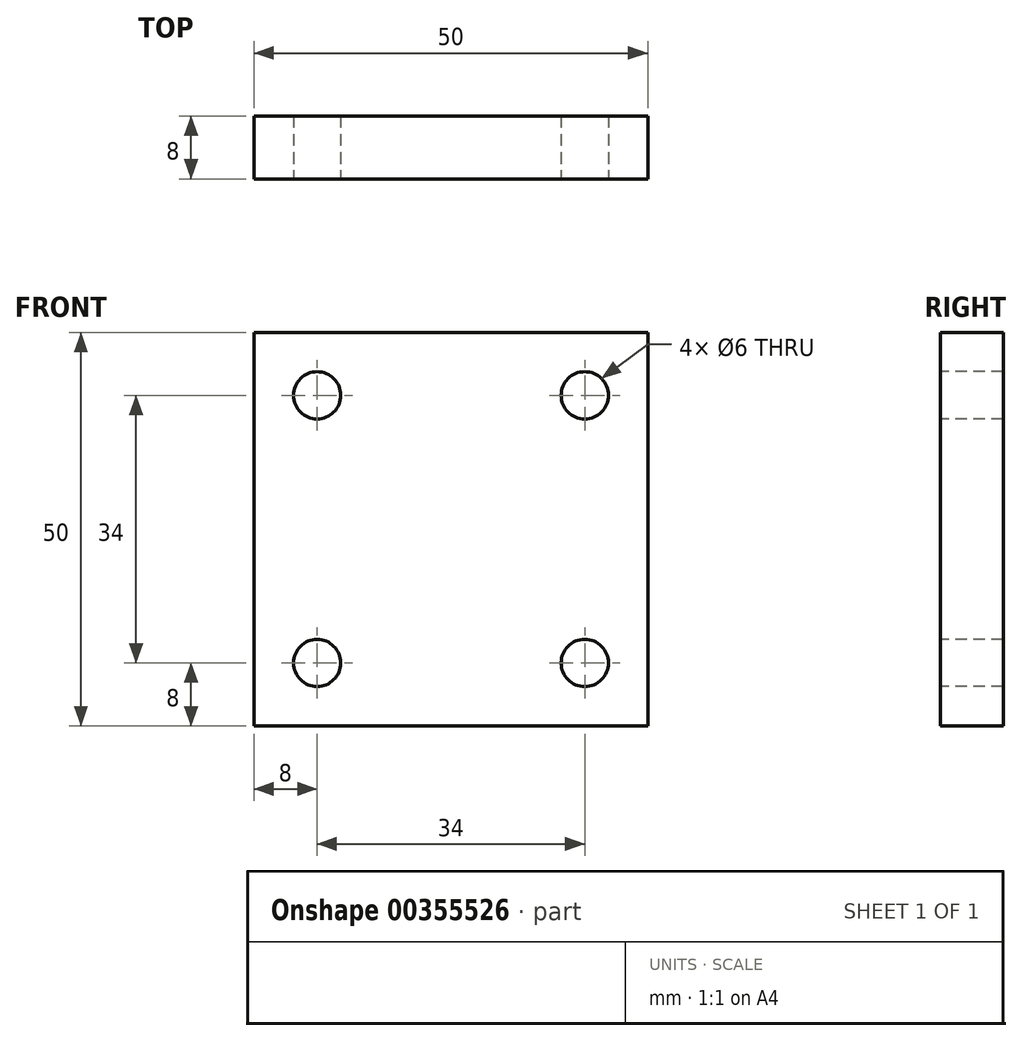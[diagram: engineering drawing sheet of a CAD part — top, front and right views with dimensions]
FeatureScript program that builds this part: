
annotation { "Feature Type Name" : "Feature", "Feature Type Description" : "" }
export const myFeature = defineFeature(function(context is Context, id is Id, definition is map)
    precondition{}
    {
        {
            var Q0;
            Q0=qCreatedBy(makeId("Front.planeOp"),FACE);
            var sketch = newSketch(context, id + "F0", { "sketchPlane" : qUnion([Q0])});
            skLineSegment(sketch, "E0.bottom", {"start": v(25, -25) * mm, "end": v(-25, -25) * mm});
            skLineSegment(sketch, "E0.top", {"start": v(25, 25) * mm, "end": v(-25, 25) * mm});
            skLineSegment(sketch, "E0.left", {"start": v(25, -25) * mm, "end": v(25, 25) * mm});
            skLineSegment(sketch, "E0.right", {"start": v(-25, -25) * mm, "end": v(-25, 25) * mm});
            skPoint(sketch, "E0.middle", {"position": v(0, 0) * mm});
            skSolve(sketch);
        }
        {
            var Q0;
            Q0 = qSketchRegion(id + "F0", true);
            extrude(context, id + "F1", {"entities" : qUnion([Q0]), "oppositeDirection" : true, "depth" : 8 * mm});
        }
        {
            var Q0;
            Q0=makeQuery(id+"F1.opExtrude","CAP_FACE",FACE,{"disambiguationData":[OSD([sQuery(id+"F0.wireOp",EDGE,"E0.bottom"),sQuery(id+"F0.wireOp",EDGE,"E0.top"),sQuery(id+"F0.wireOp",EDGE,"E0.left"),sQuery(id+"F0.wireOp",EDGE,"E0.right")])],"isStart":true});
            var sketch = newSketch(context, id + "F2", { "sketchPlane" : qUnion([Q0])});
            skCircle(sketch, "E1", {"center": v(17, 17) * mm, "radius": 3 * mm});
            skLineSegment(sketch, "E2", {"start": v(-25, 0) * mm, "end": v(25, 0) * mm, "construction": true});
            skLineSegment(sketch, "E3", {"start": v(0, 25) * mm, "end": v(0, -25) * mm, "construction": true});
            skCircle(sketch, "E4.MirrorC", {"center": v(-17, 17) * mm, "radius": 3 * mm});
            skCircle(sketch, "E5.MirrorC", {"center": v(17, -17) * mm, "radius": 3 * mm});
            skCircle(sketch, "E6.MirrorC", {"center": v(-17, -17) * mm, "radius": 3 * mm});
            skSolve(sketch);
        }
        {
            var Q0;
            Q0 = qSketchRegion(id + "F2", true);
            extrude(context, id + "F3", {"entities" : qUnion([Q0]), "operationType" : NewBodyOperationType.REMOVE, "endBound" : BoundingType.THROUGH_ALL, "oppositeDirection" : true, "depth" : 25 * mm});
        }
    });
